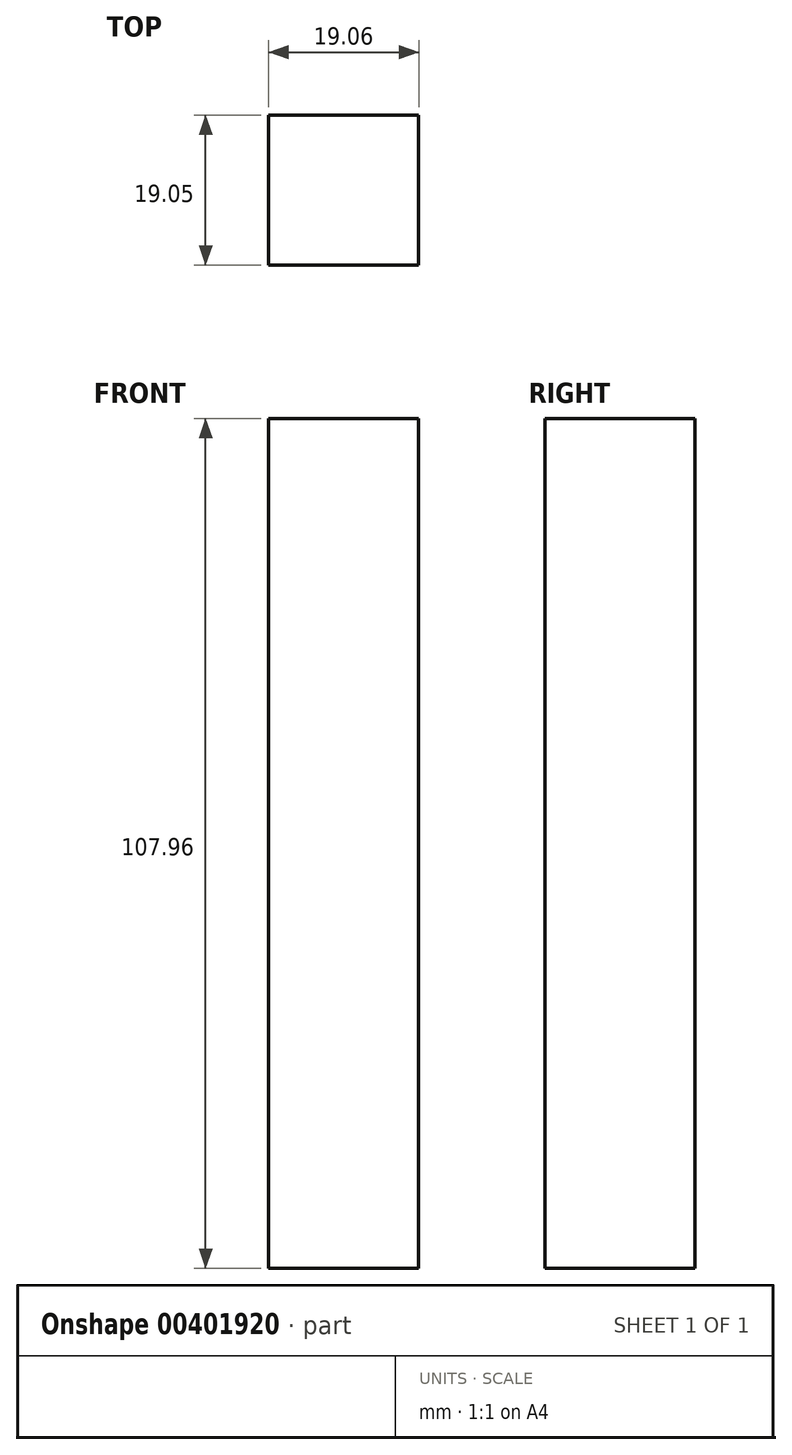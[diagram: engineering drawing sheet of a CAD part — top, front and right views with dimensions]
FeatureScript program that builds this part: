
annotation { "Feature Type Name" : "Feature", "Feature Type Description" : "" }
export const myFeature = defineFeature(function(context is Context, id is Id, definition is map)
    precondition{}
    {
        {
            var Q0;
            Q0=qCreatedBy(makeId("Front.planeOp"),FACE);
            var sketch = newSketch(context, id + "F0", { "sketchPlane" : qUnion([Q0])});
            skLineSegment(sketch, "E0.bottom", {"start": v(9.52, -53.98) * mm, "end": v(-9.53, -53.98) * mm});
            skLineSegment(sketch, "E0.top", {"start": v(9.53, 53.97) * mm, "end": v(-9.52, 53.97) * mm});
            skLineSegment(sketch, "E0.left", {"start": v(9.52, -53.98) * mm, "end": v(9.53, 53.97) * mm});
            skLineSegment(sketch, "E0.right", {"start": v(-9.53, -53.98) * mm, "end": v(-9.52, 53.97) * mm});
            skPoint(sketch, "E0.middle", {"position": v(0, 0) * mm});
            skSolve(sketch);
        }
        {
            var Q0;
            Q0=qSketchRegion(id+"F0",true);
            extrude(context, id + "F1", {"entities" : qUnion([Q0]), "depth" : 19.05 * mm});
        }
    });
